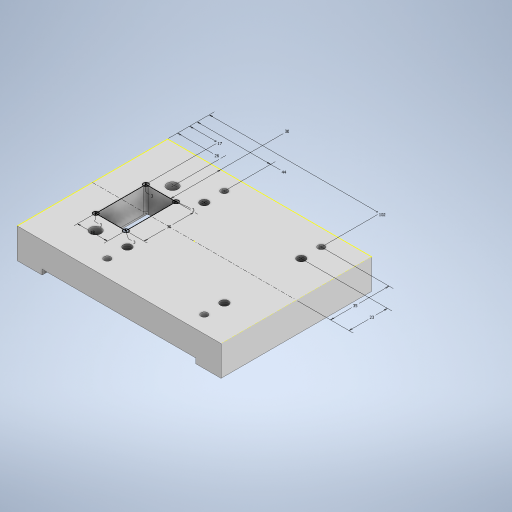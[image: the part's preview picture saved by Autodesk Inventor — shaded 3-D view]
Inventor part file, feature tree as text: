
AUTODESK INVENTOR PART (.ipt)
format: ipt  version: 2023 (Build 270158000, 158)  size: 302,592 bytes
history: native  units: mm
features: sketch x3, hole x3, pattern_linear x3, extrude x2
ambient origin geometry x8: Origin, YZ Plane, XZ Plane, XY Plane, X Axis, Y Axis, Z Axis, Center Point
bodies: Solido1 (feature_tree)
feature tree (11):
  extrude  "Estrusione1"  Depth=122.0mm
  sketch  "Schizzo4"
  extrude  "Estrusione2"  Depth=92.0mm
  hole  "Foro1"  [1 undecoded]
  hole  "Foro2"  [1 undecoded]
  pattern_linear  "Serie rettangolare1"  Count1=9 Spacing1=0.0mm
  pattern_linear  "Serie rettangolare2"  Spacing1=17.0mm  [1 undecoded]
  hole  "Foro3"  [1 undecoded]
  pattern_linear  "Serie rettangolare3"  Spacing1=18.0mm  [1 undecoded]
  sketch  "Schizzo3"
  sketch  "Schizzo5"
note: 5 required parameter values undecoded (feature->parameter linkage not recoverable at this tier; creation-order binding heuristic only, values carry confidence <= 0.55)
